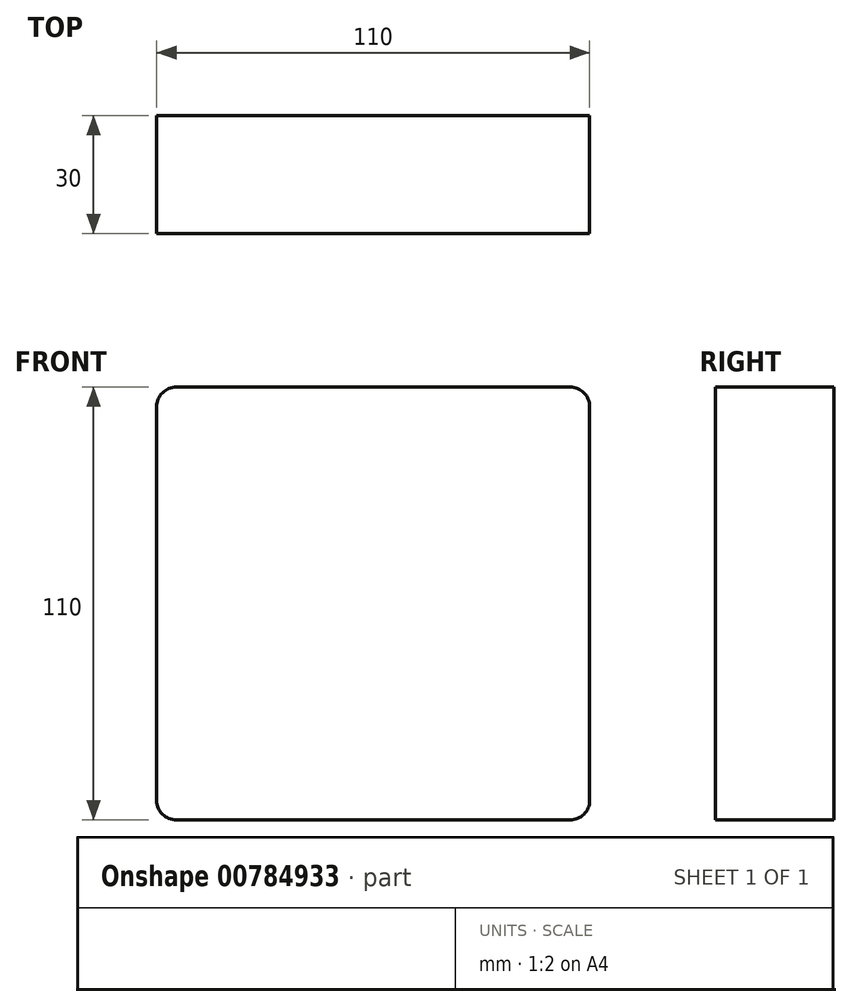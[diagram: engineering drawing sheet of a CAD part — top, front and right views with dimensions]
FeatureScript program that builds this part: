
annotation { "Feature Type Name" : "Feature", "Feature Type Description" : "" }
export const myFeature = defineFeature(function(context is Context, id is Id, definition is map)
    precondition{}
    {
        {
            var Q0;
            Q0=qCreatedBy(makeId("Front.planeOp"),FACE);
            var sketch = newSketch(context, id + "F0", { "sketchPlane" : qUnion([Q0])});
            skLineSegment(sketch, "E0.bottom", {"start": v(-55, 55) * mm, "end": v(55, 55) * mm});
            skLineSegment(sketch, "E0.top", {"start": v(-55, -55) * mm, "end": v(55, -55) * mm});
            skLineSegment(sketch, "E0.left", {"start": v(-55, 55) * mm, "end": v(-55, -55) * mm});
            skLineSegment(sketch, "E0.right", {"start": v(55, 55) * mm, "end": v(55, -55) * mm});
            skPoint(sketch, "E0.middle", {"position": v(0, 0) * mm});
            skSolve(sketch);
        }
        {
            var Q0;
            Q0 = qSketchRegion(id + "F0", true);
            extrude(context, id + "F1", {"entities" : qUnion([Q0]), "depth" : 30 * mm, "offsetDistance" : 25 * mm});
        }
        {
            var Q0;
            Q0=makeQuery(id+"F1.opExtrude","SWEPT_EDGE",EDGE,{"disambiguationData":[OSD([sQuery(id+"F0.wireOp",EDGE,"E0.top"),sQuery(id+"F0.wireOp",EDGE,"E0.right")])]});
            var Q1;
            Q1=makeQuery(id+"F1.opExtrude","SWEPT_EDGE",EDGE,{"disambiguationData":[OSD([sQuery(id+"F0.wireOp",EDGE,"E0.bottom"),sQuery(id+"F0.wireOp",EDGE,"E0.right")])]});
            var Q2;
            Q2=makeQuery(id+"F1.opExtrude","SWEPT_EDGE",EDGE,{"disambiguationData":[OSD([sQuery(id+"F0.wireOp",EDGE,"E0.top"),sQuery(id+"F0.wireOp",EDGE,"E0.left")])]});
            var Q3;
            Q3=makeQuery(id+"F1.opExtrude","SWEPT_EDGE",EDGE,{"disambiguationData":[OSD([sQuery(id+"F0.wireOp",EDGE,"E0.bottom"),sQuery(id+"F0.wireOp",EDGE,"E0.left")])]});
            fillet(context, id + "F2", {"entities" : qUnion([Q0, Q1, Q2, Q3]), "radius" : 5 * mm, "tangentPropagation" : true, "allowEdgeOverflow" : false});
        }
    });
